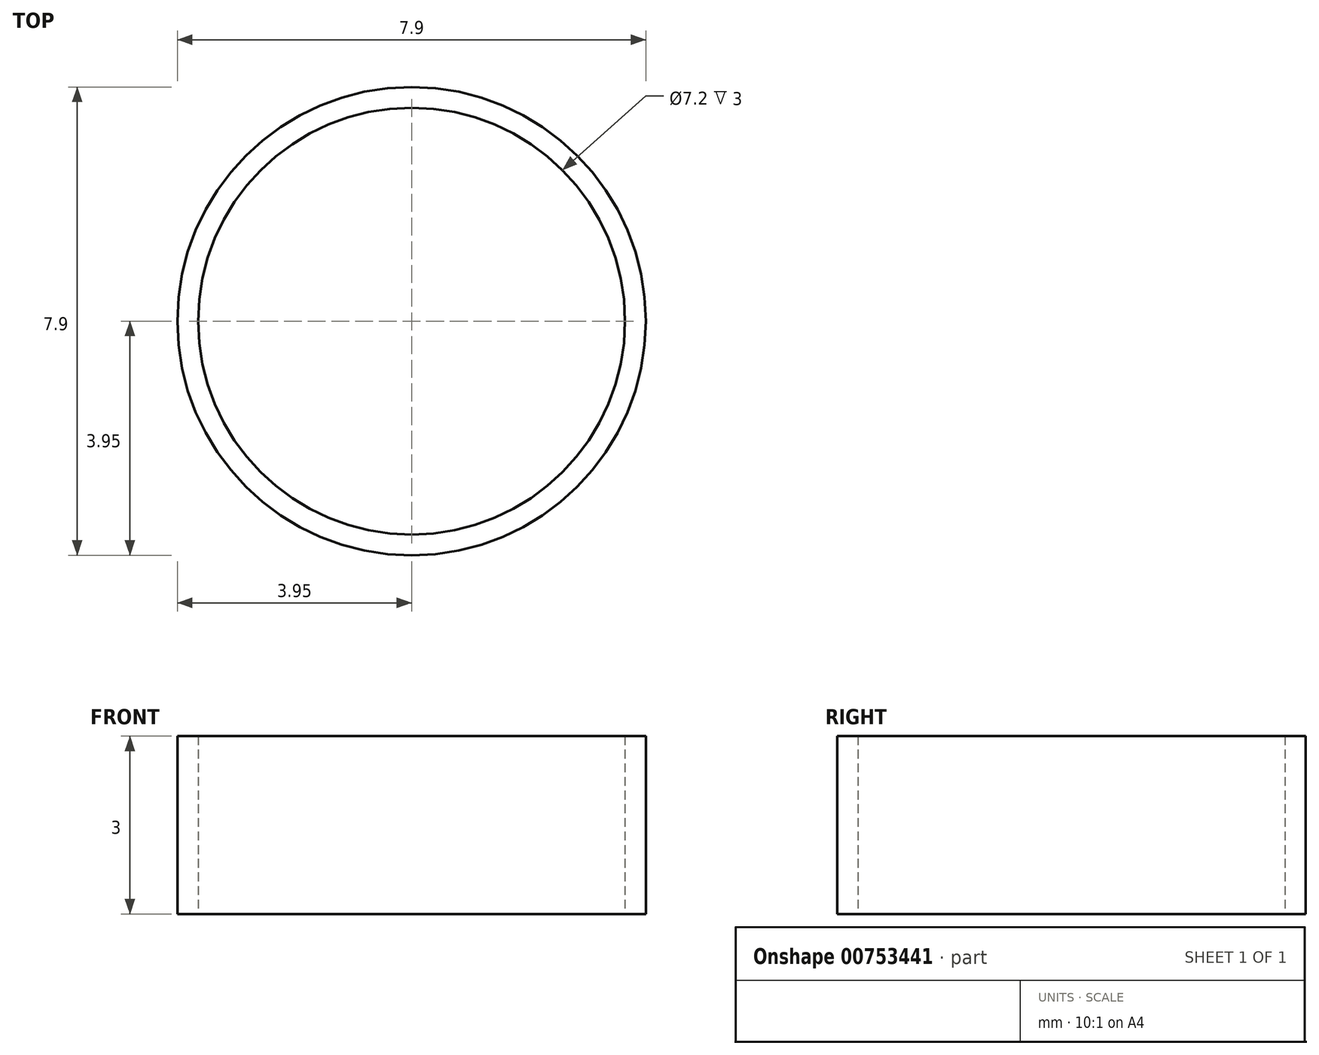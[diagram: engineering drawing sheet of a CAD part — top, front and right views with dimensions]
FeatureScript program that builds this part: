
annotation { "Feature Type Name" : "Feature", "Feature Type Description" : "" }
export const myFeature = defineFeature(function(context is Context, id is Id, definition is map)
    precondition{}
    {
        {
            var Q0;
            Q0=qCreatedBy(makeId("Top.planeOp"),FACE);
            var sketch = newSketch(context, id + "F0", { "sketchPlane" : qUnion([Q0])});
            skCircle(sketch, "E0", {"center": v(0, 0) * mm, "radius": 3.95 * mm});
            skCircle(sketch, "E1", {"center": v(0, 0) * mm, "radius": 3.6 * mm});
            skSolve(sketch);
        }
        {
            var Q0;
            Q0 = qSketchRegion(id + "F0", true);
            extrude(context, id + "F1", {"entities" : qUnion([Q0]), "depth" : 3 * mm, "offsetDistance" : 25 * mm});
        }
    });
